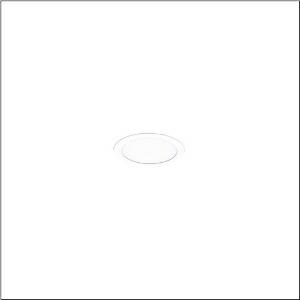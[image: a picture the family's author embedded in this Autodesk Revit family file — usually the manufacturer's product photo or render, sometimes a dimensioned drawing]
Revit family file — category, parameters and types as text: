
# Revit family: lunis_21_s_51db16ma91c
name_source: partatom
category: Lighting Fixtures
units: mm (PartAtom-declared; Revit-internal decimal feet)

## family parameters
Cut with Voids When Loaded = No
Host = Face
Light Source = No
Part Type = Normal
Room Calculation Point = No
Round Connector Dimension = Use Diameter
Shared = No

## types (1)
- --- (1 x LED, 790 lm, 5.9 W, 6500K)
    Apparent Load = 6 VA
    CIE Flux Codes = 50 80 96 100 100
    Color Rendering = 80
    Color Temperature = 6500K
    Default Elevation = 1800 mm
    Description = Lunis 21,  S, downlight, light control with lens, of PMMA, optical cover: cover panel, of PC, opal, light emission: direct distribution, LED rated luminous flux: 800lm, light colour: 830/840/865, with terminal, 3-pole, mains connection: 220..240V, AC, 50..60Hz, housing, round, of diecast aluminium, traffic white (RAL 9016), diameter: 84mm, clamping range: 1..40mm, protection rating (complete): IP20, protection rating (on room side): IP54, insulation class (complete): insulation class II (safety insulation), certification: CE, impact resistance: IK03, packaging unit: 1 piece
    Height = 0 mm  [stored 0 ft]
    Lamp = 1 x LED
    Lamp Light Flux = 790 lm
    Lamp Power = 5.9 W
    Lamp count = 1
    Length = 84 mm
    Luminous efficacy = 134 lm/W
    Manufacturer = Siteco
    ModVariant = No
    Model = 51DB16MA91C
    Mounting Place = Ceiling
    Mounting Type = Recessed
    Number of Poles = 1
    OnlyDefault = Yes
    Power Factor = 1
    Product Name = Lunis 21 S
    Product group = downlight
    ProductGroupID = 401
    Protection Class = Protection class II
    Protection Degree = IP 20
    RLX_Detail_Level = 1
    RLX_Emergency_Light_Flux = 0 lm
    RLX_Emergency_Type = 0
    RLX_Emergency_Type_DB = No
    RlxData = <blob elided: 7693 chars, md5=836fc9e6>
    Socket = socket
    Standby Power = 0 W
    System Light Flux = 790 lm
    System Power = 6 W
    Type Comments = individual setting: colour temperature 6500K
    Type Image = l_1290838.jpg
    URL = http://relux.com
    VarID = @adj_041059
    Voltage = 0 V
    Weight = 0.00 kg
    Width = 0 mm  [stored 0 ft]

note: [stored X ft] marks values corroborated as IEEE doubles in the binary element streams (Revit-internal decimal feet)

## geometry (parser evidence)
native form markers: Sweep x10
no freeform markers — native parametric forms only
